# Revit family: Furniture_Chairs-Stools-Benches_KUMI_Straw-Pall_EN
name_source: partatom
category: Furniture
revit_build: Autodesk Revit 2018 (Build: 20180329_1100(x64)
units: mm (PartAtom-declared; Revit-internal decimal feet)

## family parameters
Always vertical = No
Cut with Voids When Loaded = No
OmniClass Number = 23.21.23.13.11
OmniClass Title = Residential Chairs
Room Calculation Point = No
Shared = No
Work Plane-Based = Yes

## types (3) — shared parameters
BIMobject category = Chairs, Stools & Benches
Default Elevation = 1219.2 mm  [stored 4 ft]
Description = Straw pall - High and low
Design country = Sweden
Edition number = 1
Frame Material = Kumi - Steel - Black
Frame Material Possibility = Gray or Black
Legs Material = Kumi - Steel - Black
Legs Material Possibility = Black
Manufacturer = KUMI
Manufacturer country = Sweden
Manufacturer name = KUMI
Material main = Plywood
Material secondary = Laminate
Product Guid = 7cf2ad7f-8844-487e-928f-c15f05ebad1b
Product SKU = straw-pall-kumi
Product data url = https://bimobject.com
Product family = Straw
Product group = Stools
Product name = Straw Pall
Product url = https://www.kumi.se
QR code = https://bimobject.com
Seat Material Side = Kumi- Wood - Ash
Seat Material Side Possibility = Ash
Seat Material Top = Kumi - Laminate - Black
Seat Material Top Possibility = Ash, Gray or Black
URL = https://www.kumi.se

## per-type parameters (varying)
| type | Model |
| Type - (Straw pall 450 mm) | Straw pall 450 mm |
| Type - (Straw pall 650 mm) | Straw pall 650 mm |
| Type - (Straw pall 750 mm) | Straw pall 750 mm |

type visibility flags (boolean, named after types; folded from table):
- Type - (Straw pall 450 mm): Yes: Type - (Straw pall 450 mm)
- Type - (Straw pall 650 mm): Yes: Type - (Straw pall 650 mm), Type - (Straw pall 750 mm)_1
- Type - (Straw pall 750 mm): Yes: Type - (Straw pall 750 mm), Type - (Straw pall 750 mm)_1

note: [stored X ft] marks values corroborated as IEEE doubles in the binary element streams (Revit-internal decimal feet)

## geometry (parser evidence)
native form markers: Sweep x3
no freeform markers — native parametric forms only
